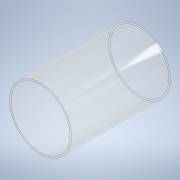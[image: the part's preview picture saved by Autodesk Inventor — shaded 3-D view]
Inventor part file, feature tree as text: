
AUTODESK INVENTOR PART (.ipt)
format: ipt  version: 2022 (Build 260153000, 153)  size: 121,856 bytes
history: native  units: in
note: dims shown in document units (in); Inventor stores cm internally (conversion verified against a paired STEP export)
features: extrude x1, sketch x1, other x1
ambient origin geometry x8: Origin, YZ Plane, XZ Plane, XY Plane, X Axis, Y Axis, Z Axis, Center Point
bodies: Solid1 (feature_tree)
feature tree (3):
  extrude  "Extrusion1"  [1 undecoded]
  sketch  "Sketch1"  dims[d0=8.4173in d1=0.0in]
  other  "Boss-Extrude1"
note: 1 required parameter value undecoded (feature->parameter linkage not recoverable at this tier; creation-order binding heuristic only, values carry confidence <= 0.55)
